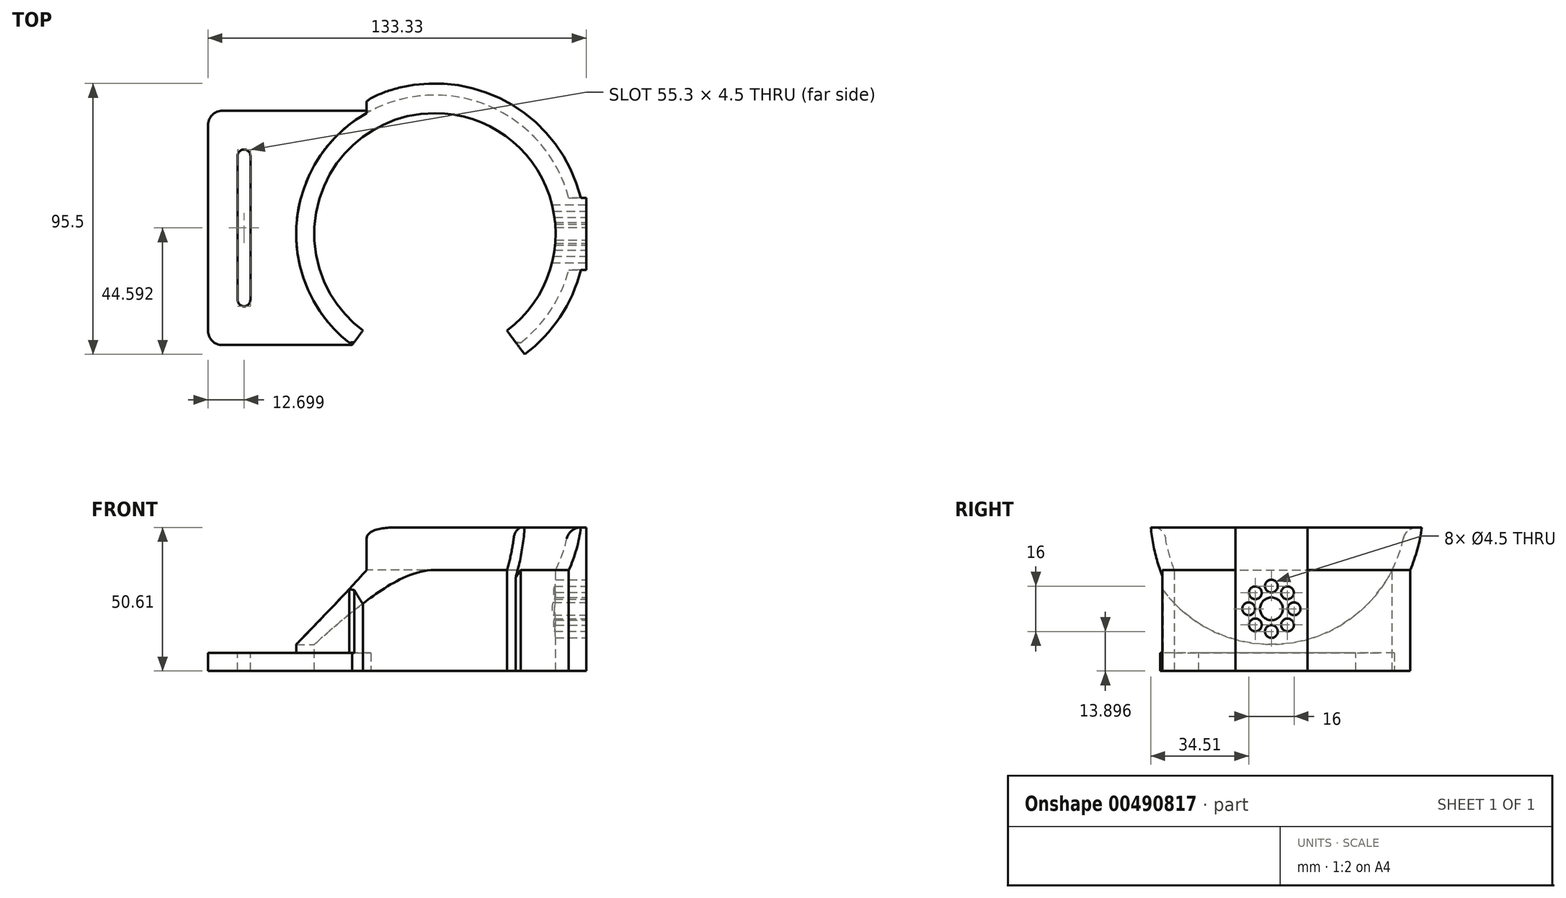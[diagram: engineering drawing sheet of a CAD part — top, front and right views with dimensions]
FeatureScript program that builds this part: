
annotation { "Feature Type Name" : "Feature", "Feature Type Description" : "" }
export const myFeature = defineFeature(function(context is Context, id is Id, definition is map)
    precondition{}
    {
        {
            var Q0;
            Q0=qCreatedBy(makeId("Top.planeOp"),FACE);
            var sketch = newSketch(context, id + "F0", { "sketchPlane" : qUnion([Q0])});
            skCircle(sketch, "E0", {"center": v(0, 0) * mm, "radius": 48.9 * mm});
            skSolve(sketch);
        }
        {
            var Q0;
            Q0=qSketchRegion(id+"F0",true);
            extrude(context, id + "F1", {"entities" : qUnion([Q0]), "depth" : 35.56 * mm});
        }
        {
            var Q0;
            Q0=makeQuery(id+"F1.opExtrude","CAP_FACE",FACE,{"disambiguationData":[OSD([sQuery(id+"F0.wireOp",EDGE,"E0")])],"isStart":false});
            var sketch = newSketch(context, id + "F2", { "sketchPlane" : qUnion([Q0])});
            skCircle(sketch, "E1", {"center": v(0, 0) * mm, "radius": 42.55 * mm});
            skSolve(sketch);
        }
        {
            var Q0;
            Q0=qSketchRegion(id+"F2",true);
            extrude(context, id + "F3", {"entities" : qUnion([Q0]), "operationType" : NewBodyOperationType.REMOVE, "endBound" : BoundingType.THROUGH_ALL, "oppositeDirection" : true, "depth" : 25.4 * mm});
        }
        {
            var Q0;
            Q0=qCreatedBy(makeId("Right.planeOp"),FACE);
            cPlane(context, id + "F4", {"entities" : qUnion([Q0]), "cplaneType" : CPlaneType.OFFSET, "offset" : 53.34 * mm, "width" : 152.4 * mm, "height" : 152.4 * mm});
        }
        {
            var Q0;
            Q0=qCreatedBy(makeId("Right.planeOp"),FACE);
            var sketch = newSketch(context, id + "F5", { "sketchPlane" : qUnion([Q0])});
            skCircle(sketch, "E2", {"center": v(0, 56.96) * mm, "radius": 47.63 * mm});
            skPoint(sketch, "E3.0", {"position": v(0, 35.56) * mm});
            skLineSegment(sketch, "E4", {"start": v(0, 0) * mm, "end": v(0, 35.56) * mm, "construction": true});
            skLineSegment(sketch, "E5.0", {"start": v(-42.55, 35.56) * mm, "end": v(42.55, 35.56) * mm, "construction": true});
            skSolve(sketch);
        }
        {
            var Q0;
            Q0=qCreatedBy(makeId("Right.planeOp"),FACE);
            var sketch = newSketch(context, id + "F6", { "sketchPlane" : qUnion([Q0])});
            skArc(sketch, "E6.0", {"start": v(-47.2, 50.61) * mm, "mid": v(-45.5, 42.9) * mm, "end": v(-42.55, 35.56) * mm});
            skLineSegment(sketch, "E7", {"start": v(-47.2, 50.61) * mm, "end": v(-53, 50.61) * mm});
            skArc(sketch, "E8", {"start": v(-53, 50.61) * mm, "mid": v(-51.5, 42.94) * mm, "end": v(-48.9, 35.56) * mm});
            skLineSegment(sketch, "E9", {"start": v(-48.9, 35.56) * mm, "end": v(-42.55, 35.56) * mm});
            skLineSegment(sketch, "E10", {"start": v(0, 56.96) * mm, "end": v(0, 38.66) * mm, "construction": true});
            skSolve(sketch);
        }
        {
            var Q0;
            Q0 = qSketchRegion(id + "F6", true);
            var Q1;
            Q1=sQuery(id+"F6.wireOp",EDGE,"E10");
            revolve(context, id + "F7", {"operationType" : NewBodyOperationType.ADD, "entities" : qUnion([Q0]), "axis" : qUnion([Q1]), "revolveType" : RevolveType.FULL});
        }
        {
            var Q0;
            Q0=qCreatedBy(id+"F4.planeOp",FACE);
            var sketch = newSketch(context, id + "F8", { "sketchPlane" : qUnion([Q0])});
            skLineSegment(sketch, "E11.bottom", {"start": v(-12.7, 0) * mm, "end": v(12.7, 0) * mm});
            skLineSegment(sketch, "E11.top", {"start": v(-12.7, 50.61) * mm, "end": v(12.7, 50.61) * mm});
            skLineSegment(sketch, "E11.left", {"start": v(-12.7, 0) * mm, "end": v(-12.7, 50.61) * mm});
            skLineSegment(sketch, "E11.right", {"start": v(12.7, 0) * mm, "end": v(12.7, 50.61) * mm});
            skPoint(sketch, "E12", {"position": v(0, 0) * mm});
            skPoint(sketch, "E13", {"position": v(0, 50.61) * mm});
            skSolve(sketch);
        }
        {
            var Q0;
            Q0=qSketchRegion(id+"F8",true);
            var Q1;
            Q1=makeQuery(id+"F1.opExtrude","SWEPT_FACE",FACE,{"disambiguationData":[OSD([sQuery(id+"F0.wireOp",EDGE,"E0")])]});
            extrude(context, id + "F9", {"entities" : qUnion([Q0]), "operationType" : NewBodyOperationType.ADD, "endBound" : BoundingType.UP_TO_NEXT, "oppositeDirection" : true, "endBoundEntityFace" : qUnion([Q1]), "depth" : 25.4 * mm});
        }
        {
            var Q0;
            Q0=makeQuery(id+"F9.opExtrude","CAP_FACE",FACE,{"disambiguationData":[OSD([sQuery(id+"F8.wireOp",EDGE,"E11.bottom"),sQuery(id+"F8.wireOp",EDGE,"E11.top"),sQuery(id+"F8.wireOp",EDGE,"E11.left"),sQuery(id+"F8.wireOp",EDGE,"E11.right")])],"isStart":true});
            var sketch = newSketch(context, id + "F10", { "sketchPlane" : qUnion([Q0])});
            skCircle(sketch, "E14", {"center": v(0, 21.9) * mm, "radius": 8 * mm, "construction": true});
            skCircle(sketch, "E15", {"center": v(0, 29.9) * mm, "radius": 2.25 * mm});
            skCircle(sketch, "E16.1.0", {"center": v(-5.66, 27.55) * mm, "radius": 2.25 * mm});
            skCircle(sketch, "E16.2.0", {"center": v(-8, 21.9) * mm, "radius": 2.25 * mm});
            skCircle(sketch, "E16.3.0", {"center": v(-5.66, 16.24) * mm, "radius": 2.25 * mm});
            skCircle(sketch, "E16.4.0", {"center": v(0, 13.9) * mm, "radius": 2.25 * mm});
            skCircle(sketch, "E16.5.0", {"center": v(5.66, 16.24) * mm, "radius": 2.25 * mm});
            skCircle(sketch, "E16.6.0", {"center": v(8, 21.9) * mm, "radius": 2.25 * mm});
            skCircle(sketch, "E16.7.0", {"center": v(5.66, 27.55) * mm, "radius": 2.25 * mm});
            skCircle(sketch, "E17", {"center": v(0, 21.9) * mm, "radius": 4 * mm});
            skSolve(sketch);
        }
        {
            var Q0;
            Q0=qSketchRegion(id+"F10",true);
            extrude(context, id + "F11", {"entities" : qUnion([Q0]), "operationType" : NewBodyOperationType.REMOVE, "endBound" : BoundingType.UP_TO_NEXT, "oppositeDirection" : true, "depth" : 25.4 * mm});
        }
        {
            var Q0;
            Q0=makeQuery(id+"F7.opRevolve","SWEPT_FACE",FACE,{"disambiguationData":[OSD([sQuery(id+"F6.wireOp",EDGE,"E7")])]});
            var sketch = newSketch(context, id + "F12", { "sketchPlane" : qUnion([Q0])});
            skLineSegment(sketch, "E18.bottom", {"start": v(-25.4, -34.13) * mm, "end": v(25.4, -34.13) * mm});
            skLineSegment(sketch, "E18.top", {"start": v(-50.32, -67.62) * mm, "end": v(50.32, -67.62) * mm});
            skLineSegment(sketch, "E18.left", {"start": v(-25.4, -34.13) * mm, "end": v(-50.32, -67.62) * mm});
            skLineSegment(sketch, "E18.right", {"start": v(25.4, -34.13) * mm, "end": v(50.32, -67.62) * mm});
            skPoint(sketch, "E19", {"position": v(0, -34.13) * mm});
            skSolve(sketch);
        }
        {
            var Q0;
            Q0=qSketchRegion(id+"F12",true);
            extrude(context, id + "F13", {"entities" : qUnion([Q0]), "operationType" : NewBodyOperationType.REMOVE, "endBound" : BoundingType.THROUGH_ALL, "oppositeDirection" : true, "depth" : 25.4 * mm});
        }
        {
            var Q0;
            Q0=qCreatedBy(makeId("Top.planeOp"),FACE);
            var sketch = newSketch(context, id + "F14", { "sketchPlane" : qUnion([Q0])});
            skArc(sketch, "E20.1", {"start": v(-18.58, 38.27) * mm, "mid": v(-42.36, 4) * mm, "end": v(-25.4, -34.13) * mm});
            skLineSegment(sketch, "E21", {"start": v(-29.2, -39.23) * mm, "end": v(-80, -39.23) * mm});
            skLineSegment(sketch, "E22", {"start": v(-80, -39.23) * mm, "end": v(-80, 43.39) * mm});
            skLineSegment(sketch, "E23", {"start": v(-80, 43.39) * mm, "end": v(-18.58, 43.39) * mm});
            skLineSegment(sketch, "E24", {"start": v(-18.58, 38.27) * mm, "end": v(-18.58, 43.39) * mm});
            skLineSegment(sketch, "E25.0", {"start": v(-25.4, -34.13) * mm, "end": v(-29.2, -39.23) * mm});
            skSolve(sketch);
        }
        {
            var Q0;
            Q0=qSketchRegion(id+"F14",true);
            extrude(context, id + "F15", {"entities" : qUnion([Q0]), "operationType" : NewBodyOperationType.ADD, "depth" : 6.35 * mm});
        }
        {
            var Q0;
            Q0 = qSketchRegion(id + "F5", true);
            extrude(context, id + "F16", {"entities" : qUnion([Q0]), "operationType" : NewBodyOperationType.REMOVE, "endBound" : BoundingType.THROUGH_ALL, "oppositeDirection" : true, "depth" : 25.4 * mm});
        }
        {
            var Q0;
            Q0=makeQuery(id+"F15.opExtrude","CAP_FACE",FACE,{"disambiguationData":[OSD([sQuery(id+"F14.wireOp",EDGE,"E20.0"),sQuery(id+"F14.wireOp",EDGE,"E20.1"),sQuery(id+"F14.wireOp",EDGE,"5v4Bg4vG-3r1A-bJ1c-4t2M-8izmqqOaVD9u"),sQuery(id+"F14.wireOp",EDGE,"E21"),sQuery(id+"F14.wireOp",EDGE,"E22"),sQuery(id+"F14.wireOp",EDGE,"E23")])],"isStart":false});
            var sketch = newSketch(context, id + "F17", { "sketchPlane" : qUnion([Q0])});
            skCircle(sketch, "E26", {"center": v(-67.3, 27.48) * mm, "radius": 2.25 * mm, "construction": true});
            skCircle(sketch, "E27", {"center": v(-67.3, -23.32) * mm, "radius": 2.25 * mm, "construction": true});
            skCircle(sketch, "E28", {"center": v(-67.3, 2.08) * mm, "radius": 2.25 * mm, "construction": true});
            skLineSegment(sketch, "E29", {"start": v(-67.3, 27.48) * mm, "end": v(-67.3, -23.32) * mm, "construction": true});
            skLineSegment(sketch, "E30", {"start": v(-67.3, 2.08) * mm, "end": v(-80, 2.08) * mm, "construction": true});
            skArc(sketch, "E31.0.startCap", {"start": v(-69.54, 27.48) * mm, "mid": v(-67.3, 29.73) * mm, "end": v(-65.04, 27.48) * mm});
            skArc(sketch, "E31.0.endCap", {"start": v(-65.04, -23.32) * mm, "mid": v(-67.3, -25.57) * mm, "end": v(-69.54, -23.32) * mm});
            skLineSegment(sketch, "E31.0.left", {"start": v(-65.04, 27.48) * mm, "end": v(-65.04, -23.32) * mm});
            skLineSegment(sketch, "E31.0.right", {"start": v(-69.54, 27.48) * mm, "end": v(-69.54, -23.32) * mm});
            skSolve(sketch);
        }
        {
            var Q0;
            Q0 = qSketchRegion(id + "F17", true);
            extrude(context, id + "F18", {"entities" : qUnion([Q0]), "operationType" : NewBodyOperationType.REMOVE, "endBound" : BoundingType.THROUGH_ALL, "oppositeDirection" : true, "depth" : 25.4 * mm});
        }
        {
            var Q0;
            Q0=makeQuery(id+"F15.opExtrude","SWEPT_EDGE",EDGE,{"disambiguationData":[OSD([sQuery(id+"F14.wireOp",EDGE,"E22"),sQuery(id+"F14.wireOp",EDGE,"E23")])]});
            var Q1;
            Q1=makeQuery(id+"F15.opExtrude","SWEPT_EDGE",EDGE,{"disambiguationData":[OSD([sQuery(id+"F14.wireOp",EDGE,"E21"),sQuery(id+"F14.wireOp",EDGE,"E22")])]});
            var Q2;
            Q2=makeQuery(id+"F16.boolean.opBoolean","INTERSECT",EDGE,{"derivedFrom":[makeQuery(id+"F9.boolean.opBoolean","MERGE",FACE,{"derivedFrom":[makeQuery(id+"F7.opRevolve","SWEPT_FACE",FACE,{"disambiguationData":[OSD([sQuery(id+"F6.wireOp",EDGE,"E7")])]}),makeQuery(id+"F9.opExtrude","SWEPT_FACE",FACE,{"disambiguationData":[OSD([sQuery(id+"F8.wireOp",EDGE,"E11.top")])]})]}),makeQuery(id+"F16.opExtrude","SWEPT_FACE",FACE,{"disambiguationData":[OSD([sQuery(id+"F5.wireOp",EDGE,"E2")])]})]});
            var Q3;
            Q3=makeQuery(id+"F16.boolean.opBoolean","INTERSECT",EDGE,{"derivedFrom":[makeQuery(id+"F9.boolean.opBoolean","MERGE",FACE,{"derivedFrom":[makeQuery(id+"F7.opRevolve","SWEPT_FACE",FACE,{"disambiguationData":[OSD([sQuery(id+"F6.wireOp",EDGE,"E7")])]}),makeQuery(id+"F9.opExtrude","SWEPT_FACE",FACE,{"disambiguationData":[OSD([sQuery(id+"F8.wireOp",EDGE,"E11.top")])]})]}),makeQuery(id+"F16.opExtrude","SWEPT_FACE",FACE,{"disambiguationData":[OSD([sQuery(id+"F5.wireOp",EDGE,"E2")])]})]});
            var Q4;
            Q4=makeQuery(id+"F9.opExtrude","CAP_EDGE",EDGE,{"disambiguationData":[OSD([sQuery(id+"F8.wireOp",EDGE,"E11.left")]),topologyDisambiguationEdgeConnected([makeQuery(id+"F1.opExtrude","SWEPT_FACE",FACE,{"disambiguationData":[OSD([sQuery(id+"F0.wireOp",EDGE,"E0")])]})])],"isStart":false});
            var Q5;
            Q5=makeQuery(id+"F9.opExtrude","CAP_EDGE",EDGE,{"disambiguationData":[OSD([sQuery(id+"F8.wireOp",EDGE,"E11.right")]),topologyDisambiguationEdgeConnected([makeQuery(id+"F1.opExtrude","SWEPT_FACE",FACE,{"disambiguationData":[OSD([sQuery(id+"F0.wireOp",EDGE,"E0")])]})])],"isStart":false});
            fillet(context, id + "F19", {"entities" : qUnion([Q0, Q1, Q2, Q3, Q4, Q5]), "radius" : 5.08 * mm, "tangentPropagation" : true, "allowEdgeOverflow" : false});
        }
        {
            var Q0;
            Q0=makeQuery(id+"F15.boolean.opBoolean","SPLIT",EDGE,{"derivedFrom":makeQuery(id+"F13.boolean.opBoolean","INTERSECT",EDGE,{"derivedFrom":[makeQuery(id+"F1.opExtrude","SWEPT_FACE",FACE,{"disambiguationData":[OSD([sQuery(id+"F0.wireOp",EDGE,"E0")])]}),makeQuery(id+"F13.opExtrude","SWEPT_FACE",FACE,{"disambiguationData":[OSD([sQuery(id+"F12.wireOp",EDGE,"E18.left")])]})]})});
            var Q1;
            Q1=makeQuery(id+"F13.boolean.opBoolean","COPY",EDGE,{"derivedFrom":makeQuery(id+"F13.opExtrude","SWEPT_EDGE",EDGE,{"disambiguationData":[OSD([sQuery(id+"F2.wireOp",EDGE,"E1"),sQuery(id+"F12.wireOp",EDGE,"E18.bottom"),sQuery(id+"F12.wireOp",EDGE,"E18.left")])]})});
            var Q2;
            Q2=makeQuery(id+"F13.boolean.opBoolean","COPY",EDGE,{"derivedFrom":makeQuery(id+"F13.opExtrude","SWEPT_EDGE",EDGE,{"disambiguationData":[OSD([sQuery(id+"F2.wireOp",EDGE,"E1"),sQuery(id+"F12.wireOp",EDGE,"E18.bottom"),sQuery(id+"F12.wireOp",EDGE,"E18.right")])]})});
            var Q3;
            Q3=makeQuery(id+"F13.boolean.opBoolean","INTERSECT",EDGE,{"derivedFrom":[makeQuery(id+"F1.opExtrude","SWEPT_FACE",FACE,{"disambiguationData":[OSD([sQuery(id+"F0.wireOp",EDGE,"E0")])]}),makeQuery(id+"F13.opExtrude","SWEPT_FACE",FACE,{"disambiguationData":[OSD([sQuery(id+"F12.wireOp",EDGE,"E18.right")])]})]});
            chamfer(context, id + "F20", {"entities" : qUnion([Q0, Q1, Q2, Q3]), "width" : 1.27 * mm, "tangentPropagation" : true});
        }
    });
